# Revit family: Foundation-Barrier-Pango-Wrap-Termite-And-Vapor_Barrier
name_source: partatom
category: Specialty Equipment
units: mm (PartAtom-declared; Revit-internal decimal feet)

## family parameters
Cut with Voids When Loaded = No
Host = Face
OmniClass Number = 23.25.05.21
OmniClass Title = Special Foundations
Part Type = Normal
Room Calculation Point = No
Round Connector Dimension = Use Diameter
Shared = No

## types (1)
- Pango® Wrap Termite & Vapor Barrier 15 mils
    ASTM = Meets ASTM E1745 Requirements
    BIMobject category = Waterproofing & Membranes
    Brand url = http://www.stegoindustries.com
    Date of publishing = 10/4/2019
    Default Elevation = 0' - 0"
    Description = "Pango Wrap Termite/Vapor Barrier is a physical barrier against Formosan termites and moisture vapor. Through patented and trade secret processes, Pango Wrap combines uniquely designed barrier materials with the flexibility and strength of extruded high-performance polyolefin film into an easy to install, physical barrier against subterranean termites. 
Stego Industries, LLC is the exclusive Representative for all products, including Pango® Wrap, Drago® Wrap and all accessory products associated with both Wrap lines owned by Stego Technology, LLC, a wholly independent company from Stego Industries, LLC. "
    Design country = United States
    Edition number = 1
    Installation instructions = https://www.stegoindustries.com
https://www.stegoindustries.com
https://www.stegoindustries.com
    Low Emitting Material = Yes
    Manufacturer = Stego Industries, LLC
    Manufacturer country = United States
    Manufacturer name = Stego Industries, LLC
    Masterformat 2014 Code = 31 31 16
    Masterformat 2014 Description = Vapor & Termite Retarders
    Material main = Polyethylene
    Max Length Note = Maximum roll length is 140'.
    Model = Pango® Wrap Termite & Vapor Barrier
    Nominal height = 0' - 0"
    Nominal width = 0' - 0"
    Product Documentation Link = https://www.stegoindustries.com
    Product Guid = https://www.stegoindustries.com
    Product Page URL = https://www.stegoindustries.com
    Product SKU = stego008
    Product certification = https://www.stegoindustries.com
    Product data url = https://bimobject.com
    Product family = Thermal and Moisture Protective Products / Pango Wrap Termite and Vapor Barrier
    Product group = Pango Wrap Vapor & Termite Barrier
    Product url = https://www.stegoindustries.com
https://www.stegoindustries.com
https://www.stegoindustries.com
    QR code = https://bimobject.com
    Stego Vapor Barrier = Pango® Wrap Termite & Vapor  Barrier
    Technical description = Physical barrier to subterranean termites and under-slab vapor barrier
    URL = http://www.stegoindustries.com
    Vapor Barrier Thickness = 15 mils
    Weight Net (Kg) = 0
    Youtube clip = https://youtu.be

## geometry (parser evidence)
native form markers: Sweep x2
no freeform markers — native parametric forms only
